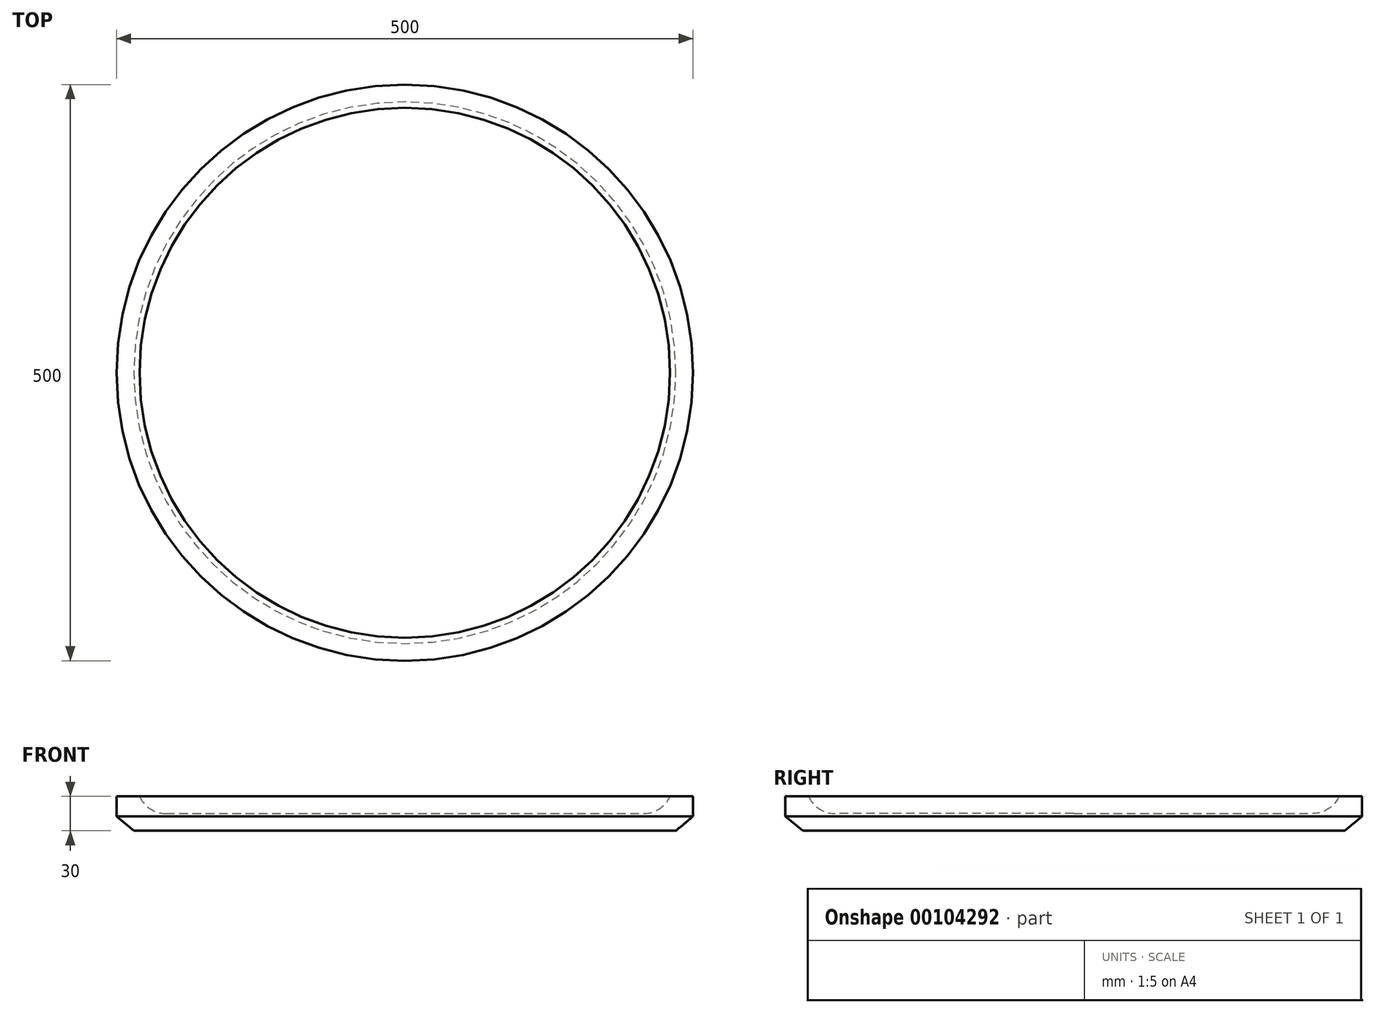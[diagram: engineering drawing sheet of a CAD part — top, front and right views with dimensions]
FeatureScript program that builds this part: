
annotation { "Feature Type Name" : "Feature", "Feature Type Description" : "" }
export const myFeature = defineFeature(function(context is Context, id is Id, definition is map)
    precondition{}
    {
        {
            var Q0;
            Q0=qCreatedBy(makeId("Front.planeOp"),FACE);
            var sketch = newSketch(context, id + "F0", { "sketchPlane" : qUnion([Q0])});
            skLineSegment(sketch, "E0", {"start": v(0, 0) * mm, "end": v(235, 0) * mm});
            skLineSegment(sketch, "E1", {"start": v(235, 0) * mm, "end": v(250, 12.59) * mm});
            skLineSegment(sketch, "E2", {"start": v(250, 12.59) * mm, "end": v(250, 30) * mm});
            skLineSegment(sketch, "E3", {"start": v(250, 30) * mm, "end": v(230, 30) * mm});
            skLineSegment(sketch, "E4", {"start": v(230, 30) * mm, "end": v(230, 15) * mm});
            skLineSegment(sketch, "E5", {"start": v(230, 15) * mm, "end": v(0, 15) * mm});
            skLineSegment(sketch, "E6", {"start": v(0, 15) * mm, "end": v(0, 0) * mm});
            skSolve(sketch);
        }
        {
            var Q0;
            Q0=makeQuery(id+"F0.imprint","IMPRINT",FACE,{"disambiguationData":[TD([[makeQuery(id+"F0.imprint","IMPRINT",EDGE,{"derivedFrom":sQuery(id+"F0.wireOp",EDGE,"E0")}),1.0]])]});
            var Q1;
            Q1=sQuery(id+"F0.wireOp",EDGE,"E6");
            revolve(context, id + "F1", {"entities" : qUnion([Q0]), "axis" : qUnion([Q1]), "revolveType" : RevolveType.FULL});
        }
        {
            var Q0;
            Q0=makeQuery(id+"F1.opRevolve","SWEPT_EDGE",EDGE,{"disambiguationData":[OSD([sQuery(id+"F0.wireOp",EDGE,"E4"),sQuery(id+"F0.wireOp",EDGE,"E5")])]});
            fillet(context, id + "F2", {"entities" : qUnion([Q0]), "radius" : 25 * mm, "tangentPropagation" : true, "allowEdgeOverflow" : false});
        }
    });
